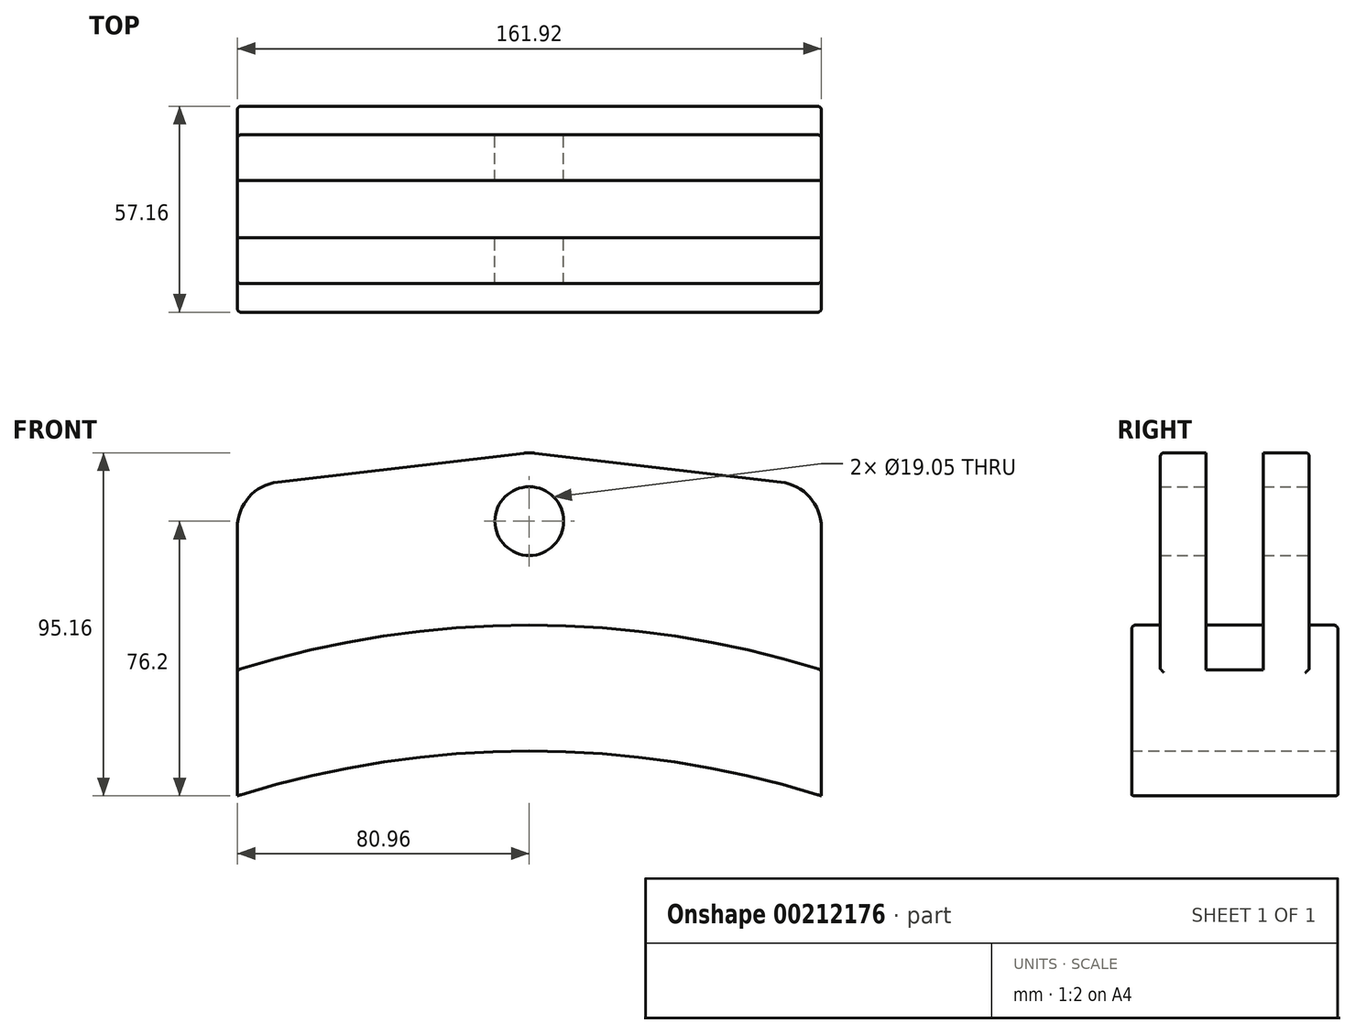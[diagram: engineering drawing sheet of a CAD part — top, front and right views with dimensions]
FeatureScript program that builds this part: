
annotation { "Feature Type Name" : "Feature", "Feature Type Description" : "" }
export const myFeature = defineFeature(function(context is Context, id is Id, definition is map)
    precondition{}
    {
        {
            var Q0;
            Q0=qCreatedBy(makeId("Front.planeOp"),FACE);
            var sketch = newSketch(context, id + "F0", { "sketchPlane" : qUnion([Q0])});
            skLineSegment(sketch, "E0", {"start": v(0, 0) * mm, "end": v(-80.96, 0) * mm, "construction": true});
            skLineSegment(sketch, "E1", {"start": v(0, 0) * mm, "end": v(80.96, 0) * mm, "construction": true});
            skArc(sketch, "E2", {"start": v(80.96, 0) * mm, "mid": v(0, 12.42) * mm, "end": v(-80.96, 0) * mm});
            skLineSegment(sketch, "E3", {"start": v(80.96, 0) * mm, "end": v(80.96, 34.93) * mm});
            skLineSegment(sketch, "E4", {"start": v(-80.96, 0) * mm, "end": v(-80.96, 34.92) * mm});
            skArc(sketch, "E5", {"start": v(80.96, 34.92) * mm, "mid": v(0, 47.34) * mm, "end": v(-80.96, 34.92) * mm});
            skLineSegment(sketch, "E6", {"start": v(80.96, 34.93) * mm, "end": v(80.96, 74.43) * mm});
            skLineSegment(sketch, "E7", {"start": v(-80.96, 34.92) * mm, "end": v(-80.96, 74.43) * mm});
            skPoint(sketch, "E8", {"position": v(0, 95.25) * mm});
            skLineSegment(sketch, "E9", {"start": v(-69.75, 87.04) * mm, "end": v(-1.48, 95.08) * mm});
            skLineSegment(sketch, "E10", {"start": v(1.48, 95.08) * mm, "end": v(69.75, 87.04) * mm});
            skPoint(sketch, "E11.visualSharp", {"position": v(-80.96, 85.73) * mm});
            skArc(sketch, "E11.filletArc", {"start": v(-69.75, 87.04) * mm, "mid": v(-77.75, 82.87) * mm, "end": v(-80.96, 74.43) * mm});
            skPoint(sketch, "E12.visualSharp", {"position": v(80.96, 85.73) * mm});
            skArc(sketch, "E12.filletArc", {"start": v(80.96, 74.43) * mm, "mid": v(77.75, 82.87) * mm, "end": v(69.75, 87.04) * mm});
            skArc(sketch, "E13.filletArc", {"start": v(1.48, 95.08) * mm, "mid": v(0, 95.16) * mm, "end": v(-1.48, 95.08) * mm});
            skCircle(sketch, "E14", {"center": v(0, 76.2) * mm, "radius": 9.53 * mm});
            skSolve(sketch);
        }
        {
            var Q0;
            Q0=makeQuery(id+"F0.imprint","IMPRINT",FACE,{"disambiguationData":[TD([[makeQuery(id+"F0.imprint","IMPRINT",EDGE,{"derivedFrom":sQuery(id+"F0.wireOp",EDGE,"E2")}),-1.0]])]});
            extrude(context, id + "F1", {"entities" : qUnion([Q0]), "endBound" : BoundingType.SYMMETRIC, "depth" : 57.15 * mm});
        }
        {
            var Q0;
            Q0=makeQuery(id+"F0.imprint","IMPRINT",FACE,{"disambiguationData":[TD([[makeQuery(id+"F0.imprint","IMPRINT",EDGE,{"derivedFrom":sQuery(id+"F0.wireOp",EDGE,"E5")}),-1.0]])]});
            extrude(context, id + "F2", {"entities" : qUnion([Q0]), "operationType" : NewBodyOperationType.ADD, "endBound" : BoundingType.SYMMETRIC, "depth" : 41.27 * mm});
        }
        {
            var Q0;
            Q0=makeQuery(id+"F0.imprint","IMPRINT",FACE,{"disambiguationData":[TD([[makeQuery(id+"F0.imprint","IMPRINT",EDGE,{"derivedFrom":sQuery(id+"F0.wireOp",EDGE,"E5")}),-1.0]])]});
            extrude(context, id + "F3", {"entities" : qUnion([Q0]), "operationType" : NewBodyOperationType.REMOVE, "endBound" : BoundingType.SYMMETRIC, "oppositeDirection" : true, "depth" : 15.88 * mm});
        }
        {
            var Q0;
            Q0=makeQuery(id+"F2.boolean.opBoolean","MERGE",FACE,{"derivedFrom":[makeQuery(id+"F1.opExtrude","SWEPT_FACE",FACE,{"disambiguationData":[OSD([sQuery(id+"F0.wireOp",EDGE,"E3")])]}),makeQuery(id+"F2.opExtrude","SWEPT_FACE",FACE,{"disambiguationData":[OSD([sQuery(id+"F0.wireOp",EDGE,"E6")])]})]});
            var sketch = newSketch(context, id + "F4", { "sketchPlane" : qUnion([Q0])});
            skLineSegment(sketch, "E15", {"start": v(-28.58, 0) * mm, "end": v(28.58, 7.02) * mm});
            skLineSegment(sketch, "E16", {"start": v(28.58, 7.02) * mm, "end": v(28.58, 0) * mm});
            skLineSegment(sketch, "E17", {"start": v(28.58, 0) * mm, "end": v(-28.58, 0) * mm});
            skSolve(sketch);
        }
        {
            var Q0;
            Q0=qCreatedBy(makeId("Top.planeOp"),FACE);
            cPlane(context, id + "F5", {"entities" : qUnion([Q0]), "cplaneType" : CPlaneType.OFFSET, "offset" : 270.2 * mm, "oppositeDirection" : true, "width" : 152.4 * mm, "height" : 152.4 * mm});
        }
        {
            var Q0;
            Q0=qCreatedBy(id+"F5.planeOp",FACE);
            var sketch = newSketch(context, id + "F6", { "sketchPlane" : qUnion([Q0])});
            skLineSegment(sketch, "E18", {"start": v(0, 0) * mm, "end": v(0, -77.19) * mm, "construction": true});
            skSolve(sketch);
        }
        {
            var Q0;
            {var subQ0=sQuery(id+"F0.wireOp",EDGE,"E6");var subQ1=sQuery(id+"F0.wireOp",EDGE,"E5");var subQ2=sQuery(id+"F0.wireOp",EDGE,"E3");Q0=makeQuery(id+"F2.boolean.opBoolean","SPLIT",EDGE,{"disambiguationData":[TD([makeQuery(id+"F1.opExtrude","CAP_FACE",FACE,{"disambiguationData":[OSD([sQuery(id+"F0.wireOp",EDGE,"E2"),subQ2,sQuery(id+"F0.wireOp",EDGE,"E4"),subQ1])],"isStart":true})])],"derivedFrom":makeQuery(id+"F1.opExtrude","SWEPT_EDGE",EDGE,{"disambiguationData":[OSD([subQ2,subQ1,subQ0])]})});}
            var Q1;
            {var subQ0=sQuery(id+"F0.wireOp",EDGE,"E6");var subQ1=sQuery(id+"F0.wireOp",EDGE,"E5");var subQ2=sQuery(id+"F0.wireOp",EDGE,"E3");Q1=makeQuery(id+"F2.boolean.opBoolean","SPLIT",EDGE,{"disambiguationData":[TD([makeQuery(id+"F1.opExtrude","CAP_FACE",FACE,{"disambiguationData":[OSD([sQuery(id+"F0.wireOp",EDGE,"E2"),subQ2,sQuery(id+"F0.wireOp",EDGE,"E4"),subQ1])],"isStart":false})])],"derivedFrom":makeQuery(id+"F1.opExtrude","SWEPT_EDGE",EDGE,{"disambiguationData":[OSD([subQ2,subQ1,subQ0])]})});}
            var Q2;
            {var subQ0=sQuery(id+"F0.wireOp",EDGE,"E7");var subQ1=sQuery(id+"F0.wireOp",EDGE,"E5");var subQ2=sQuery(id+"F0.wireOp",EDGE,"E4");Q2=makeQuery(id+"F2.boolean.opBoolean","SPLIT",EDGE,{"disambiguationData":[TD([makeQuery(id+"F1.opExtrude","CAP_FACE",FACE,{"disambiguationData":[OSD([sQuery(id+"F0.wireOp",EDGE,"E2"),sQuery(id+"F0.wireOp",EDGE,"E3"),subQ2,subQ1])],"isStart":true})])],"derivedFrom":makeQuery(id+"F1.opExtrude","SWEPT_EDGE",EDGE,{"disambiguationData":[OSD([subQ2,subQ1,subQ0])]})});}
            var Q3;
            {var subQ0=sQuery(id+"F0.wireOp",EDGE,"E7");var subQ1=sQuery(id+"F0.wireOp",EDGE,"E5");var subQ2=sQuery(id+"F0.wireOp",EDGE,"E4");Q3=makeQuery(id+"F2.boolean.opBoolean","SPLIT",EDGE,{"disambiguationData":[TD([makeQuery(id+"F1.opExtrude","CAP_FACE",FACE,{"disambiguationData":[OSD([sQuery(id+"F0.wireOp",EDGE,"E2"),sQuery(id+"F0.wireOp",EDGE,"E3"),subQ2,subQ1])],"isStart":false})])],"derivedFrom":makeQuery(id+"F1.opExtrude","SWEPT_EDGE",EDGE,{"disambiguationData":[OSD([subQ2,subQ1,subQ0])]})});}
            var Q4;
            Q4=makeQuery(id+"F3.boolean.opBoolean","COPY",EDGE,{"derivedFrom":makeQuery(id+"F3.opExtrude","SWEPT_EDGE",EDGE,{"disambiguationData":[OSD([sQuery(id+"F0.wireOp",EDGE,"E4"),sQuery(id+"F0.wireOp",EDGE,"E5"),sQuery(id+"F0.wireOp",EDGE,"E7")])]})});
            var Q5;
            Q5=makeQuery(id+"F3.boolean.opBoolean","COPY",EDGE,{"derivedFrom":makeQuery(id+"F3.opExtrude","SWEPT_EDGE",EDGE,{"disambiguationData":[OSD([sQuery(id+"F0.wireOp",EDGE,"E3"),sQuery(id+"F0.wireOp",EDGE,"E5"),sQuery(id+"F0.wireOp",EDGE,"E6")])]})});
            var Q6;
            Q6=makeQuery(id+"F1.opExtrude","CAP_EDGE",EDGE,{"disambiguationData":[OSD([sQuery(id+"F0.wireOp",EDGE,"E3")])],"isStart":true});
            var Q7;
            Q7=makeQuery(id+"F1.opExtrude","CAP_EDGE",EDGE,{"disambiguationData":[OSD([sQuery(id+"F0.wireOp",EDGE,"E3")])],"isStart":false});
            var Q8;
            Q8=makeQuery(id+"F1.opExtrude","CAP_EDGE",EDGE,{"disambiguationData":[OSD([sQuery(id+"F0.wireOp",EDGE,"E4")])],"isStart":true});
            var Q9;
            Q9=makeQuery(id+"F1.opExtrude","CAP_EDGE",EDGE,{"disambiguationData":[OSD([sQuery(id+"F0.wireOp",EDGE,"E4")])],"isStart":false});
            var Q10;
            Q10=makeQuery(id+"F1.opExtrude","CAP_EDGE",EDGE,{"disambiguationData":[OSD([sQuery(id+"F0.wireOp",EDGE,"E5")])],"isStart":false});
            var Q11;
            Q11=makeQuery(id+"F1.opExtrude","CAP_EDGE",EDGE,{"disambiguationData":[OSD([sQuery(id+"F0.wireOp",EDGE,"E5")])],"isStart":true});
            var Q12;
            Q12=makeQuery(id+"F2.opExtrude","CAP_EDGE",EDGE,{"disambiguationData":[OSD([sQuery(id+"F0.wireOp",EDGE,"E7")])],"isStart":false});
            var Q13;
            Q13=makeQuery(id+"F3.boolean.opBoolean","COPY",EDGE,{"derivedFrom":makeQuery(id+"F3.opExtrude","CAP_EDGE",EDGE,{"disambiguationData":[OSD([sQuery(id+"F0.wireOp",EDGE,"E7")])],"isStart":true})});
            var Q14;
            Q14=makeQuery(id+"F2.opExtrude","CAP_EDGE",EDGE,{"disambiguationData":[OSD([sQuery(id+"F0.wireOp",EDGE,"E6")])],"isStart":true});
            var Q15;
            Q15=makeQuery(id+"F3.boolean.opBoolean","COPY",EDGE,{"derivedFrom":makeQuery(id+"F3.opExtrude","CAP_EDGE",EDGE,{"disambiguationData":[OSD([sQuery(id+"F0.wireOp",EDGE,"E6")])],"isStart":false})});
            fillet(context, id + "F7", {"entities" : qUnion([Q0, Q1, Q2, Q3, Q4, Q5, Q6, Q7, Q8, Q9, Q10, Q11, Q12, Q13, Q14, Q15]), "radius" : 1.02 * mm, "tangentPropagation" : true, "allowEdgeOverflow" : false});
        }
    });
